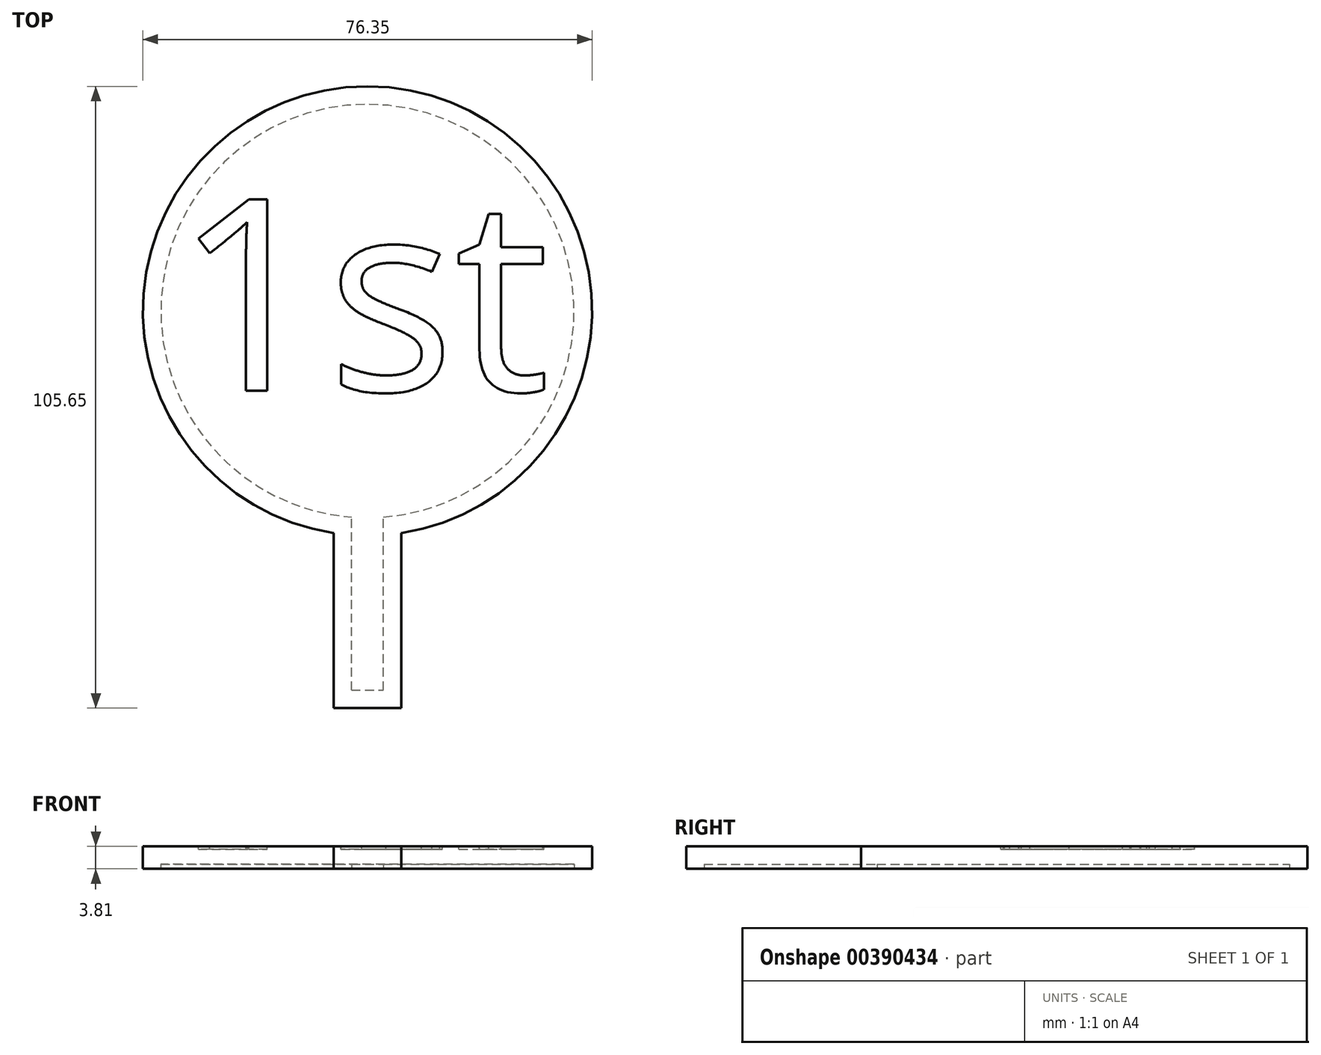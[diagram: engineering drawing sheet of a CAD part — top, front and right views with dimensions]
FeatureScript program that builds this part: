
annotation { "Feature Type Name" : "Feature", "Feature Type Description" : "" }
export const myFeature = defineFeature(function(context is Context, id is Id, definition is map)
    precondition{}
    {
        {
            var Q0;
            Q0=qCreatedBy(makeId("Top.planeOp"),FACE);
            var sketch = newSketch(context, id + "F0", { "sketchPlane" : qUnion([Q0])});
            skLineSegment(sketch, "E0", {"start": v(-13.52, -35.14) * mm, "end": v(-1.98, -35.14) * mm});
            skLineSegment(sketch, "E1", {"start": v(-1.98, -35.14) * mm, "end": v(-1.98, -5.4) * mm});
            skLineSegment(sketch, "E2", {"start": v(-13.52, -35.14) * mm, "end": v(-13.52, -5.4) * mm});
            skArc(sketch, "E3", {"start": v(-1.98, -5.4) * mm, "mid": v(-7.75, 70.5) * mm, "end": v(-13.52, -5.4) * mm});
            skSolve(sketch);
        }
        {
            var Q0;
            Q0=makeQuery(id+"F0.imprint","IMPRINT",FACE,{"disambiguationData":[TD([[makeQuery(id+"F0.imprint","IMPRINT",EDGE,{"derivedFrom":sQuery(id+"F0.wireOp",EDGE,"E0")}),1.0]])]});
            extrude(context, id + "F1", {"entities" : qUnion([Q0]), "depth" : 3.8 * mm});
        }
        {
            var Q0;
            Q0=makeQuery(id+"F1.opExtrude","CAP_FACE",FACE,{"disambiguationData":[OSD([sQuery(id+"F0.wireOp",EDGE,"E0"),sQuery(id+"F0.wireOp",EDGE,"E1"),sQuery(id+"F0.wireOp",EDGE,"E2"),sQuery(id+"F0.wireOp",EDGE,"E3")])],"isStart":true});
            shell(context, id + "F2", {"entities" : qUnion([Q0]), "thickness" : 3.05 * mm});
        }
        {
            var Q0;
            Q0=makeQuery(id+"F1.opExtrude","CAP_FACE",FACE,{"disambiguationData":[OSD([sQuery(id+"F0.wireOp",EDGE,"E0"),sQuery(id+"F0.wireOp",EDGE,"E1"),sQuery(id+"F0.wireOp",EDGE,"E2"),sQuery(id+"F0.wireOp",EDGE,"E3")])],"isStart":false});
            var sketch = newSketch(context, id + "F3", { "sketchPlane" : qUnion([Q0])});
            skText(sketch, "E4", { "text": "1st", "fontName": "OpenSans-Regular.ttf"});
            const initialGuessF3  = {"E4": [-0.0407, 0.01878, 1, 0, 0.03282]};
            skSetInitialGuess(sketch, initialGuessF3);
            skSolve(sketch);
        }
        {
            var Q0;
            Q0 = qSketchRegion(id + "F3", true);
            extrude(context, id + "F4", {"entities" : qUnion([Q0]), "operationType" : NewBodyOperationType.REMOVE, "oppositeDirection" : true, "depth" : 0.5 * mm});
        }
    });
